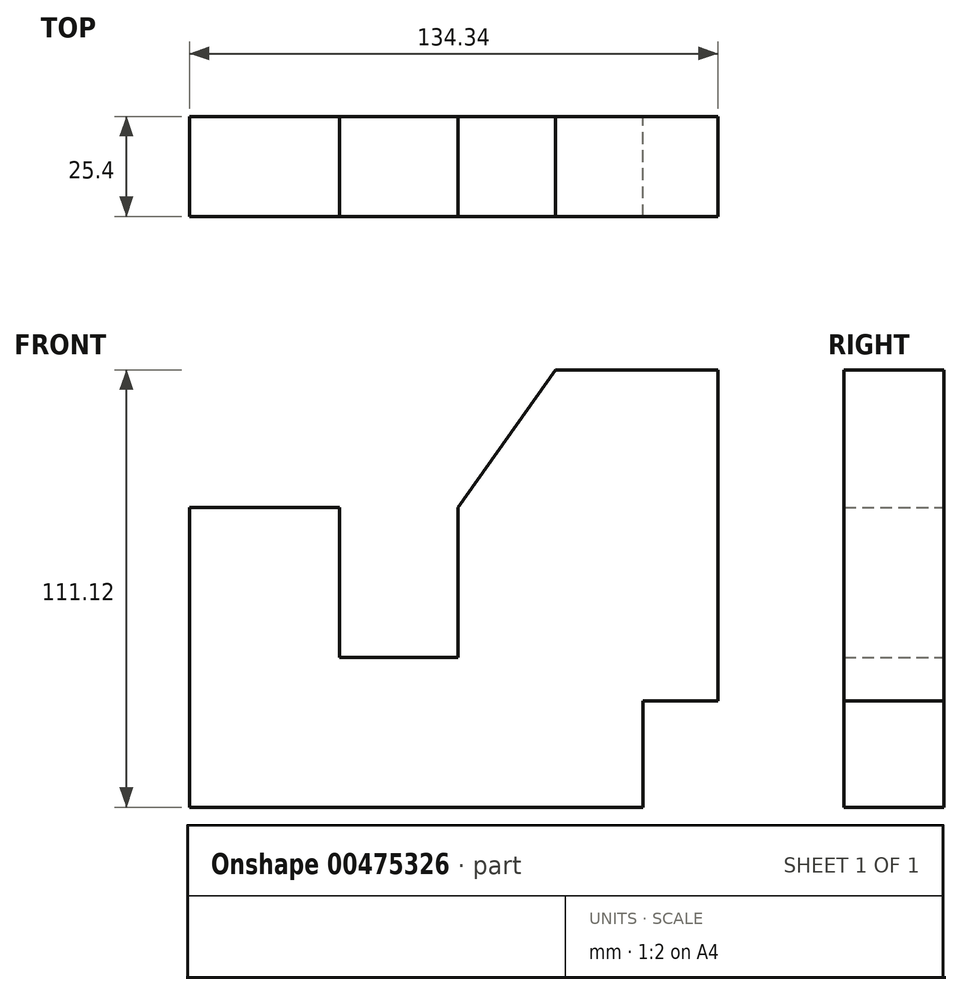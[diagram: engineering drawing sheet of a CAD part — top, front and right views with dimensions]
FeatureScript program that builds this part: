
annotation { "Feature Type Name" : "Feature", "Feature Type Description" : "" }
export const myFeature = defineFeature(function(context is Context, id is Id, definition is map)
    precondition{}
    {
        {
            var Q0;
            Q0=qCreatedBy(makeId("Front.planeOp"),FACE);
            var sketch = newSketch(context, id + "F0", { "sketchPlane" : qUnion([Q0])});
            skLineSegment(sketch, "E0", {"start": v(-57.35, 29.43) * mm, "end": v(-57.35, -46.77) * mm});
            skLineSegment(sketch, "E1", {"start": v(-57.35, -46.77) * mm, "end": v(57.94, -46.77) * mm});
            skLineSegment(sketch, "E2", {"start": v(57.94, -46.77) * mm, "end": v(57.94, -19.77) * mm});
            skLineSegment(sketch, "E3", {"start": v(57.94, -19.77) * mm, "end": v(77, -19.77) * mm});
            skLineSegment(sketch, "E4", {"start": v(77, -19.77) * mm, "end": v(77, 64.35) * mm});
            skLineSegment(sketch, "E5", {"start": v(-57.35, 29.43) * mm, "end": v(-19.25, 29.43) * mm});
            skLineSegment(sketch, "E6", {"start": v(-19.25, 29.43) * mm, "end": v(-19.25, -8.67) * mm});
            skLineSegment(sketch, "E7", {"start": v(-19.25, -8.67) * mm, "end": v(10.92, -8.67) * mm});
            skLineSegment(sketch, "E8", {"start": v(10.92, -8.67) * mm, "end": v(10.92, 29.43) * mm});
            skLineSegment(sketch, "E9", {"start": v(77, 64.35) * mm, "end": v(35.72, 64.35) * mm});
            skLineSegment(sketch, "E10", {"start": v(35.72, 64.35) * mm, "end": v(10.92, 29.43) * mm});
            skSolve(sketch);
        }
        {
            var Q0;
            Q0=makeQuery(id+"F0.imprint","IMPRINT",FACE,{"disambiguationData":[TD([[makeQuery(id+"F0.imprint","IMPRINT",EDGE,{"derivedFrom":sQuery(id+"F0.wireOp",EDGE,"E0")}),1.0]])]});
            extrude(context, id + "F1", {"entities" : qUnion([Q0]), "depth" : 25.4 * mm});
        }
    });
